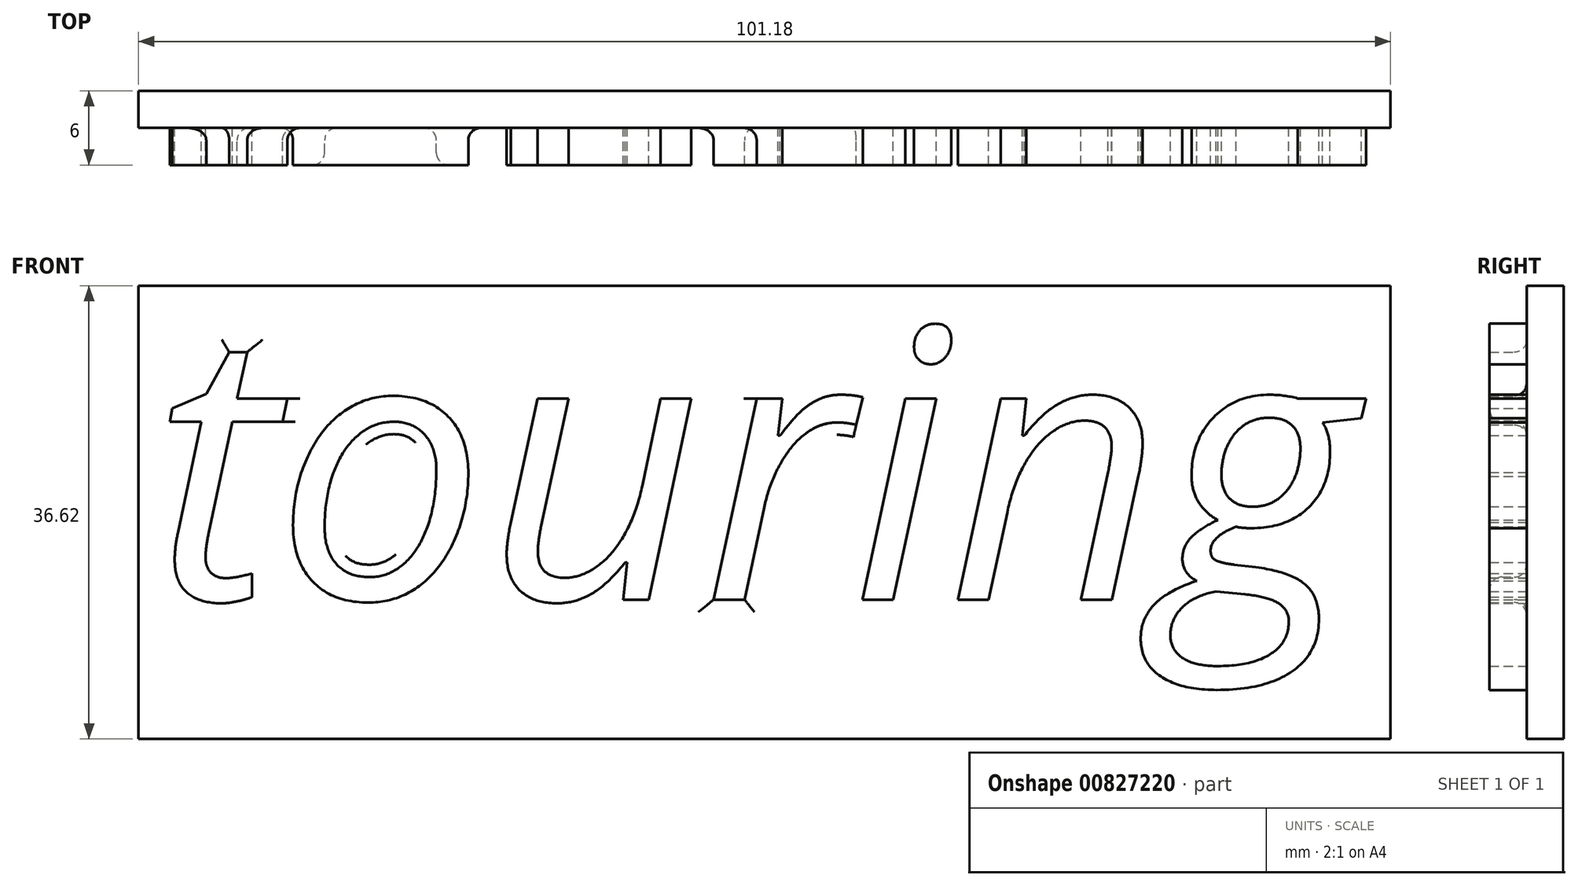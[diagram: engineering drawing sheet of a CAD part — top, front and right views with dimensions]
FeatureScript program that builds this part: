
annotation { "Feature Type Name" : "Feature", "Feature Type Description" : "" }
export const myFeature = defineFeature(function(context is Context, id is Id, definition is map)
    precondition{}
    {
        {
            var Q0;
            Q0=qCreatedBy(makeId("Front.planeOp"),FACE);
            var sketch = newSketch(context, id + "F0", { "sketchPlane" : qUnion([Q0])});
            skText(sketch, "E0", { "text": "touring", "fontName": "OpenSans-Italic.ttf"});
            const initialGuessF0  = {"E0": [-0.1, 0.01126, 1, 0, 0.02187]};
            skSetInitialGuess(sketch, initialGuessF0);
            skSolve(sketch);
        }
        {
            var Q0;
            Q0 = qSketchRegion(id + "F0", true);
            extrude(context, id + "F1", {"entities" : qUnion([Q0]), "depth" : 6 * mm, "offsetDistance" : 25 * mm});
        }
        {
            var Q0;
            Q0=qCreatedBy(makeId("Front.planeOp"),FACE);
            var sketch = newSketch(context, id + "F2", { "sketchPlane" : qUnion([Q0])});
            skLineSegment(sketch, "E1.bottom", {"start": v(0, 0) * mm, "end": v(-101.18, 0) * mm});
            skLineSegment(sketch, "E1.top", {"start": v(0, 36.62) * mm, "end": v(-101.18, 36.62) * mm});
            skLineSegment(sketch, "E1.left", {"start": v(0, 0) * mm, "end": v(0, 36.62) * mm});
            skLineSegment(sketch, "E1.right", {"start": v(-101.18, 0) * mm, "end": v(-101.18, 36.62) * mm});
            skSolve(sketch);
        }
        {
            var Q0;
            Q0=makeQuery(id+"F2.imprint","IMPRINT",FACE,{"disambiguationData":[TD([[makeQuery(id+"F2.imprint","IMPRINT",EDGE,{"derivedFrom":sQuery(id+"F2.wireOp",EDGE,"E1.bottom")}),-1.0]])]});
            extrude(context, id + "F3", {"entities" : qUnion([Q0]), "operationType" : NewBodyOperationType.ADD, "depth" : 3 * mm, "offsetDistance" : 25 * mm});
        }
        {
            var Q0;
            Q0=makeQuery(id+"F3.boolean.opBoolean","INTERSECT",EDGE,{"derivedFrom":[makeQuery(id+"F1.opExtrude","SWEPT_FACE",FACE,{"disambiguationData":[OSD([sQuery(id+"F0.wireOp",EDGE,"E0.sketch_text.stroke-15")])]}),makeQuery(id+"F3.opExtrude","CAP_FACE",FACE,{"disambiguationData":[OSD([sQuery(id+"F2.wireOp",EDGE,"E1.bottom"),sQuery(id+"F2.wireOp",EDGE,"E1.top"),sQuery(id+"F2.wireOp",EDGE,"E1.left"),sQuery(id+"F2.wireOp",EDGE,"E1.right")])],"isStart":false})]});
            var Q1;
            Q1=makeQuery(id+"F3.boolean.opBoolean","INTERSECT",EDGE,{"derivedFrom":[makeQuery(id+"F1.opExtrude","SWEPT_FACE",FACE,{"disambiguationData":[OSD([sQuery(id+"F0.wireOp",EDGE,"E0.sketch_text.stroke-34")])]}),makeQuery(id+"F3.opExtrude","CAP_FACE",FACE,{"disambiguationData":[OSD([sQuery(id+"F2.wireOp",EDGE,"E1.bottom"),sQuery(id+"F2.wireOp",EDGE,"E1.top"),sQuery(id+"F2.wireOp",EDGE,"E1.left"),sQuery(id+"F2.wireOp",EDGE,"E1.right")])],"isStart":false})]});
            var Q2;
            Q2=makeQuery(id+"F3.boolean.opBoolean","INTERSECT",EDGE,{"derivedFrom":[makeQuery(id+"F1.opExtrude","SWEPT_FACE",FACE,{"disambiguationData":[OSD([sQuery(id+"F0.wireOp",EDGE,"E0.sketch_text.stroke-22")])]}),makeQuery(id+"F3.opExtrude","CAP_FACE",FACE,{"disambiguationData":[OSD([sQuery(id+"F2.wireOp",EDGE,"E1.bottom"),sQuery(id+"F2.wireOp",EDGE,"E1.top"),sQuery(id+"F2.wireOp",EDGE,"E1.left"),sQuery(id+"F2.wireOp",EDGE,"E1.right")])],"isStart":false})]});
            var Q3;
            Q3=makeQuery(id+"F3.boolean.opBoolean","INTERSECT",EDGE,{"derivedFrom":[makeQuery(id+"F1.opExtrude","SWEPT_FACE",FACE,{"disambiguationData":[OSD([sQuery(id+"F0.wireOp",EDGE,"E0.sketch_text.stroke-11")])]}),makeQuery(id+"F3.opExtrude","CAP_FACE",FACE,{"disambiguationData":[OSD([sQuery(id+"F2.wireOp",EDGE,"E1.bottom"),sQuery(id+"F2.wireOp",EDGE,"E1.top"),sQuery(id+"F2.wireOp",EDGE,"E1.left"),sQuery(id+"F2.wireOp",EDGE,"E1.right")])],"isStart":false})]});
            var Q4;
            Q4=makeQuery(id+"F3.boolean.opBoolean","INTERSECT",EDGE,{"derivedFrom":[makeQuery(id+"F1.opExtrude","SWEPT_FACE",FACE,{"disambiguationData":[OSD([sQuery(id+"F0.wireOp",EDGE,"E0.sketch_text.stroke-12")])]}),makeQuery(id+"F3.opExtrude","CAP_FACE",FACE,{"disambiguationData":[OSD([sQuery(id+"F2.wireOp",EDGE,"E1.bottom"),sQuery(id+"F2.wireOp",EDGE,"E1.top"),sQuery(id+"F2.wireOp",EDGE,"E1.left"),sQuery(id+"F2.wireOp",EDGE,"E1.right")])],"isStart":false})]});
            var Q5;
            Q5=makeQuery(id+"F3.boolean.opBoolean","INTERSECT",EDGE,{"derivedFrom":[makeQuery(id+"F1.opExtrude","SWEPT_FACE",FACE,{"disambiguationData":[OSD([sQuery(id+"F0.wireOp",EDGE,"E0.sketch_text.stroke-13")])]}),makeQuery(id+"F3.opExtrude","CAP_FACE",FACE,{"disambiguationData":[OSD([sQuery(id+"F2.wireOp",EDGE,"E1.bottom"),sQuery(id+"F2.wireOp",EDGE,"E1.top"),sQuery(id+"F2.wireOp",EDGE,"E1.left"),sQuery(id+"F2.wireOp",EDGE,"E1.right")])],"isStart":false})]});
            var Q6;
            Q6=makeQuery(id+"F3.boolean.opBoolean","INTERSECT",EDGE,{"derivedFrom":[makeQuery(id+"F1.opExtrude","SWEPT_FACE",FACE,{"disambiguationData":[OSD([sQuery(id+"F0.wireOp",EDGE,"E0.sketch_text.stroke-68")])]}),makeQuery(id+"F3.opExtrude","CAP_FACE",FACE,{"disambiguationData":[OSD([sQuery(id+"F2.wireOp",EDGE,"E1.bottom"),sQuery(id+"F2.wireOp",EDGE,"E1.top"),sQuery(id+"F2.wireOp",EDGE,"E1.left"),sQuery(id+"F2.wireOp",EDGE,"E1.right")])],"isStart":false})]});
            var Q7;
            Q7=makeQuery(id+"F3.boolean.opBoolean","INTERSECT",EDGE,{"derivedFrom":[makeQuery(id+"F1.opExtrude","SWEPT_FACE",FACE,{"disambiguationData":[OSD([sQuery(id+"F0.wireOp",EDGE,"E0.sketch_text.stroke-66")])]}),makeQuery(id+"F3.opExtrude","CAP_FACE",FACE,{"disambiguationData":[OSD([sQuery(id+"F2.wireOp",EDGE,"E1.bottom"),sQuery(id+"F2.wireOp",EDGE,"E1.top"),sQuery(id+"F2.wireOp",EDGE,"E1.left"),sQuery(id+"F2.wireOp",EDGE,"E1.right")])],"isStart":false})]});
            var Q8;
            Q8=makeQuery(id+"F3.boolean.opBoolean","INTERSECT",EDGE,{"derivedFrom":[makeQuery(id+"F1.opExtrude","SWEPT_FACE",FACE,{"disambiguationData":[OSD([sQuery(id+"F0.wireOp",EDGE,"E0.sketch_text.stroke-67")])]}),makeQuery(id+"F3.opExtrude","CAP_FACE",FACE,{"disambiguationData":[OSD([sQuery(id+"F2.wireOp",EDGE,"E1.bottom"),sQuery(id+"F2.wireOp",EDGE,"E1.top"),sQuery(id+"F2.wireOp",EDGE,"E1.left"),sQuery(id+"F2.wireOp",EDGE,"E1.right")])],"isStart":false})]});
            var Q9;
            Q9=makeQuery(id+"F1.opExtrude","CAP_EDGE",EDGE,{"disambiguationData":[OSD([sQuery(id+"F0.wireOp",EDGE,"E0.sketch_text.stroke-39")])],"isStart":false});
            fillet(context, id + "F4", {"entities" : qUnion([Q0, Q1, Q2, Q3, Q4, Q5, Q6, Q7, Q8, Q9]), "radius" : 1 * mm, "tangentPropagation" : true, "allowEdgeOverflow" : false});
        }
    });
